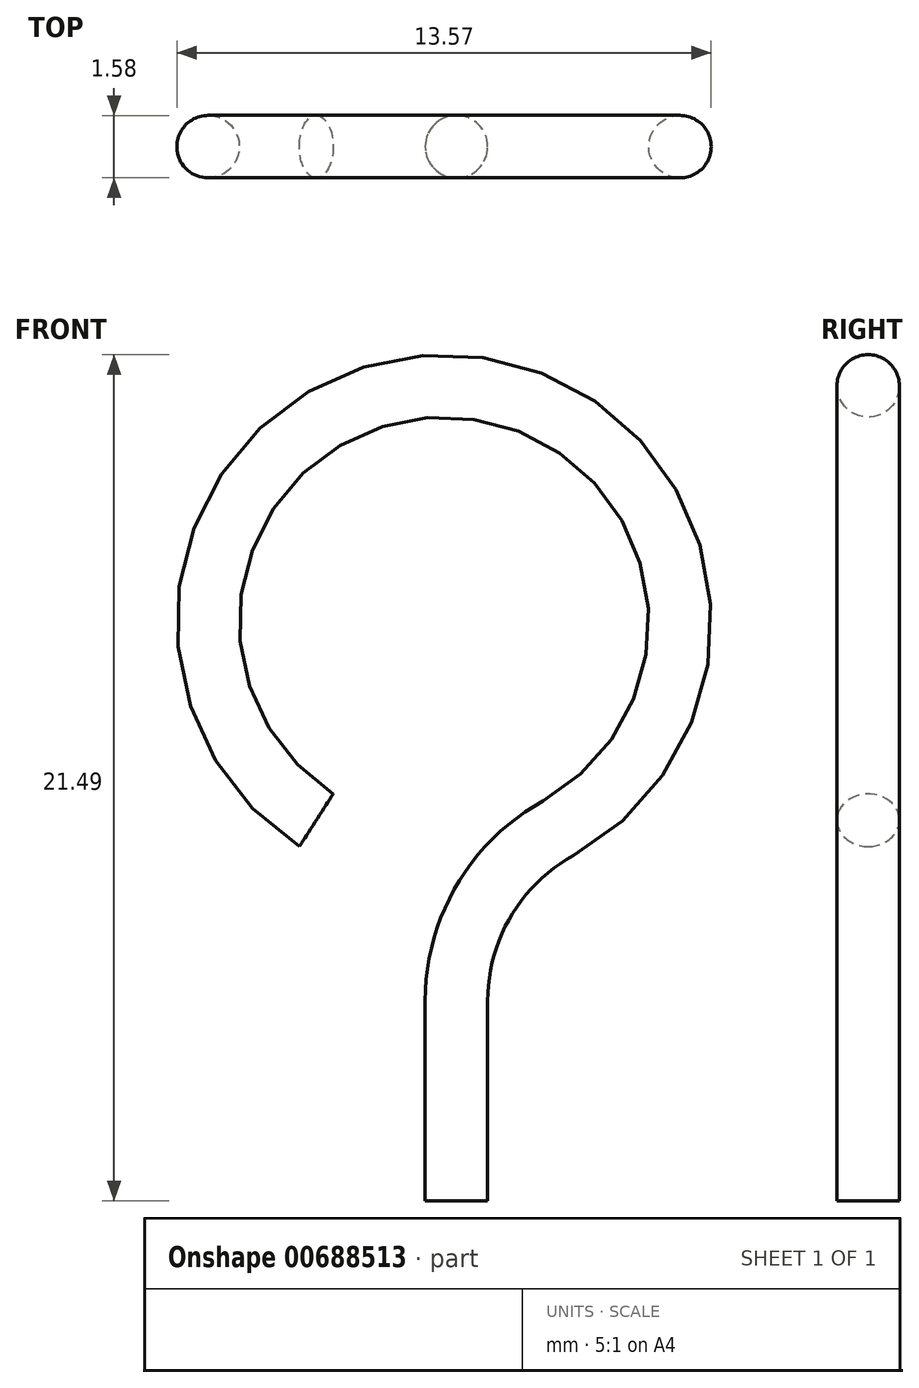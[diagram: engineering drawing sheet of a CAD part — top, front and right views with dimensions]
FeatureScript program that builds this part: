
annotation { "Feature Type Name" : "Feature", "Feature Type Description" : "" }
export const myFeature = defineFeature(function(context is Context, id is Id, definition is map)
    precondition{}
    {
        {
            var Q0;
            Q0=qCreatedBy(makeId("Top.planeOp"),FACE);
            var sketch = newSketch(context, id + "F0", { "sketchPlane" : qUnion([Q0])});
            skCircle(sketch, "E0", {"center": v(0, 0) * mm, "radius": 0.8 * mm});
            skSolve(sketch);
        }
        {
            var Q0;
            Q0=qCreatedBy(makeId("Front.planeOp"),FACE);
            var sketch = newSketch(context, id + "F1", { "sketchPlane" : qUnion([Q0])});
            skLineSegment(sketch, "E1", {"start": v(0, 0) * mm, "end": v(0, 5.08) * mm});
            skArc(sketch, "E2", {"start": v(0, 5.08) * mm, "mid": v(0.7, 7.62) * mm, "end": v(2.58, 9.46) * mm});
            skArc(sketch, "E3", {"start": v(2.58, 9.46) * mm, "mid": v(4.23, 18.61) * mm, "end": v(-5.06, 18.37) * mm});
            skArc(sketch, "E4", {"start": v(-5.06, 18.37) * mm, "mid": v(-6.22, 13.69) * mm, "end": v(-3.56, 9.67) * mm});
            skSolve(sketch);
        }
        {
            var Q0;
            Q0=makeQuery(id+"F0.imprint","IMPRINT",FACE,{"disambiguationData":[TD([[makeQuery(id+"F0.imprint","IMPRINT",EDGE,{"derivedFrom":sQuery(id+"F0.wireOp",EDGE,"E0")}),1.0]])]});
            var Q1;
            Q1=sQuery(id+"F1.wireOp",EDGE,"E1");
            var Q2;
            Q2=sQuery(id+"F1.wireOp",EDGE,"E2");
            var Q3;
            Q3=sQuery(id+"F1.wireOp",EDGE,"E3");
            var Q4;
            Q4=sQuery(id+"F1.wireOp",EDGE,"E4");
            sweep(context, id + "F2", {"profiles" : qUnion([Q0]), "path" : qUnion([Q1, Q2, Q3, Q4])});
        }
    });
